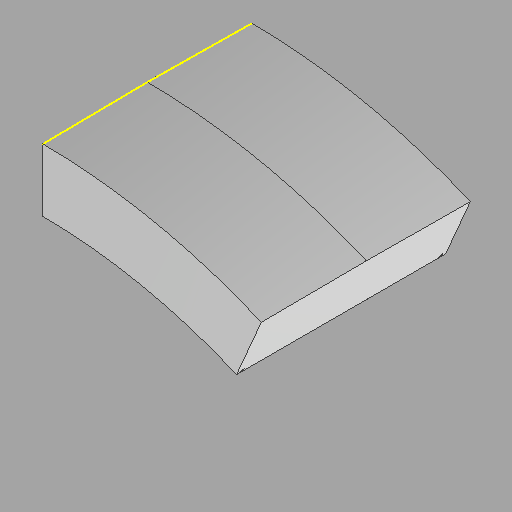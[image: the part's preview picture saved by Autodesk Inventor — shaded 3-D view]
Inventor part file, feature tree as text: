
AUTODESK INVENTOR PART (.ipt)
format: ipt  version: 2022.2 (Build 262287010, 287A)  size: 192,512 bytes
history: native  units: in
note: dims shown in document units (in); Inventor stores cm internally (conversion verified against a paired STEP export)
features: sketch x5, sweep x3, thicken_offset x2, projected_geometry x2, other x1, extrude x1
ambient origin geometry x8: Origin, YZ Plane, XZ Plane, XY Plane, X Axis, Y Axis, Z Axis, Center Point
bodies: Solid1 (feature_tree)
feature tree (14):
  other  "Cap (5)"
  sketch  "Sketch1"  dims[d0=0.25in d1=0.25in]
  sweep  "Sweep1"
  sketch  "Sketch2"  dims[d2=0.375in d3=0.25in d4=0.25in d5=0.375in d6=0.125in d7=0.0in d8=0.0in d9=1.0in d10=0.0in d11=0.0in d12=0.0in d13=0.0in d14=0.0in d21=1.0in d22=1.0in d23=1.0in d24=1.0in]
  extrude  "Extrusion1"  Depth=1.0in
  sweep  "Sweep2"
  sweep  "Sweep3"
  thicken_offset  "Thicken1"
  thicken_offset  "Thicken2"
  projected_geometry  "Projected Loop1"
  sketch  "3D Sketch1"
  projected_geometry  "Projected Loop2"
  sketch  "3D Sketch2"
  sketch  "3D Sketch3"
